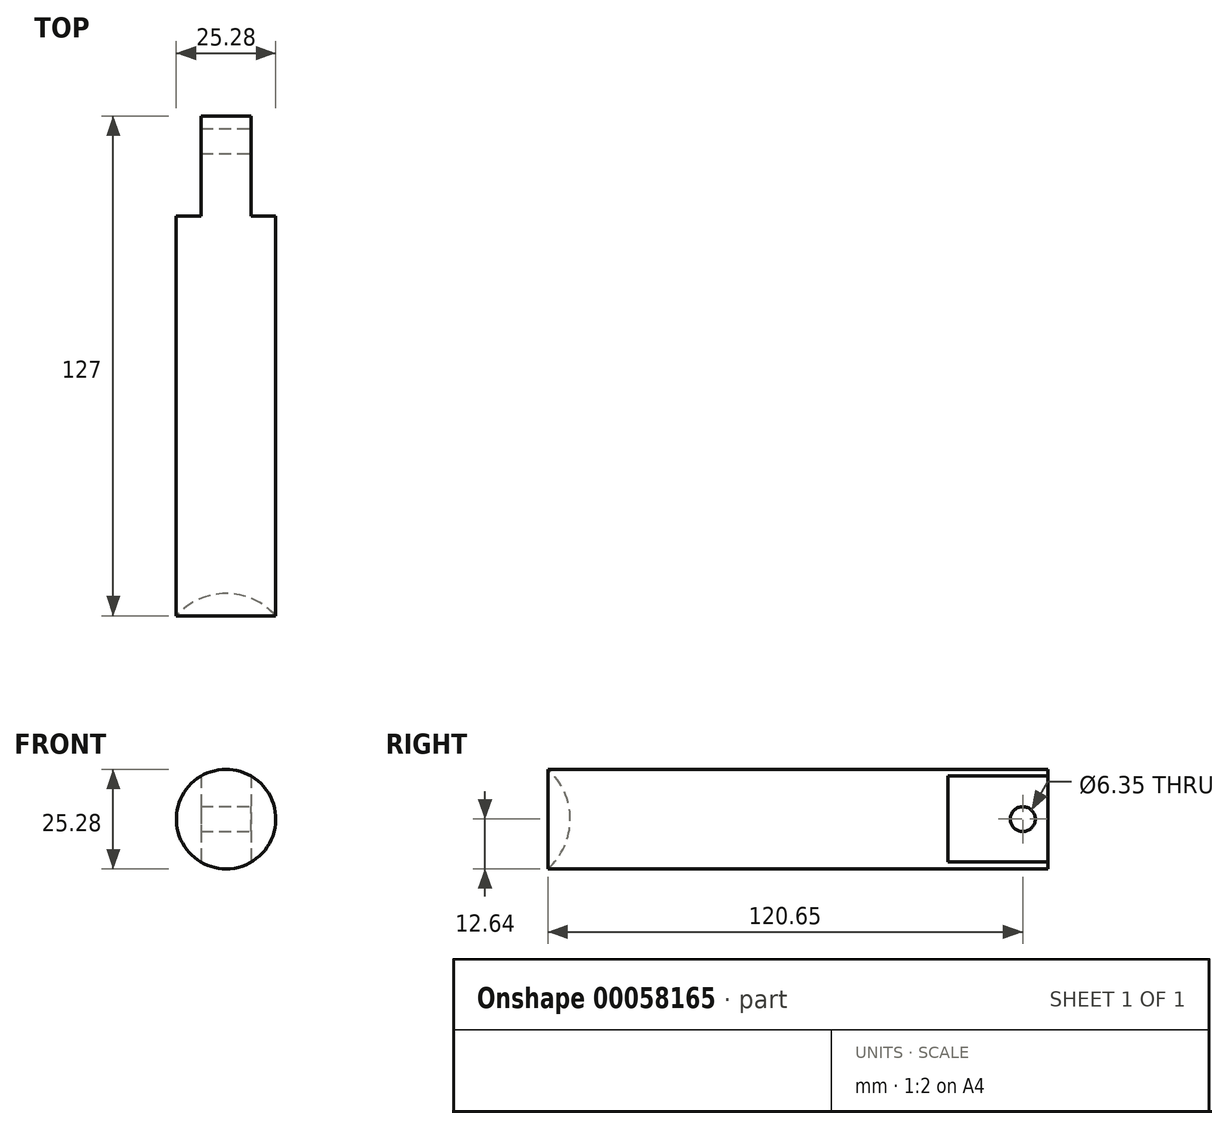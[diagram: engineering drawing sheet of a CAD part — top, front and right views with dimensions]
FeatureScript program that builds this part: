
annotation { "Feature Type Name" : "Feature", "Feature Type Description" : "" }
export const myFeature = defineFeature(function(context is Context, id is Id, definition is map)
    precondition{}
    {
        {
            var Q0;
            Q0=qCreatedBy(makeId("Front.planeOp"),FACE);
            var sketch = newSketch(context, id + "F0", { "sketchPlane" : qUnion([Q0])});
            skCircle(sketch, "E0", {"center": v(0, 0) * mm, "radius": 12.64 * mm});
            skSolve(sketch);
        }
        {
            var Q0;
            Q0=makeQuery(id+"F0.imprint","IMPRINT",FACE,{"disambiguationData":[TD([[makeQuery(id+"F0.imprint","IMPRINT",EDGE,{"derivedFrom":sQuery(id+"F0.wireOp",EDGE,"E0")}),1.0]])]});
            extrude(context, id + "F1", {"entities" : qUnion([Q0]), "depth" : 127 * mm});
        }
        {
            var Q0;
            Q0=qCreatedBy(makeId("Top.planeOp"),FACE);
            var sketch = newSketch(context, id + "F2", { "sketchPlane" : qUnion([Q0])});
            skLineSegment(sketch, "E1", {"start": v(6.35, 10.47) * mm, "end": v(6.35, -25.4) * mm});
            skLineSegment(sketch, "E2", {"start": v(6.35, -25.4) * mm, "end": v(27.52, -25.4) * mm});
            skLineSegment(sketch, "E3", {"start": v(27.52, -25.4) * mm, "end": v(27.52, 10.47) * mm});
            skLineSegment(sketch, "E4", {"start": v(27.52, 10.47) * mm, "end": v(6.35, 10.47) * mm});
            skLineSegment(sketch, "E5", {"start": v(0, 43.64) * mm, "end": v(0, 10.15) * mm, "construction": true});
            skLineSegment(sketch, "E6.MirrorCS", {"start": v(-6.35, -25.4) * mm, "end": v(-27.52, -25.4) * mm});
            skLineSegment(sketch, "E7.MirrorCS", {"start": v(-27.52, -25.4) * mm, "end": v(-27.52, 10.47) * mm});
            skLineSegment(sketch, "E8.MirrorCS", {"start": v(-6.35, 10.47) * mm, "end": v(-6.35, -25.4) * mm});
            skLineSegment(sketch, "E9.MirrorCS", {"start": v(-27.52, 10.47) * mm, "end": v(-6.35, 10.47) * mm});
            skSolve(sketch);
        }
        {
            var Q0;
            Q0=makeQuery(id+"F2.imprint","IMPRINT",FACE,{"disambiguationData":[TD([[makeQuery(id+"F2.imprint","IMPRINT",EDGE,{"derivedFrom":sQuery(id+"F2.wireOp",EDGE,"E1")}),1.0]])]});
            var Q1;
            Q1=makeQuery(id+"F2.imprint","IMPRINT",FACE,{"disambiguationData":[TD([[makeQuery(id+"F2.imprint","IMPRINT",EDGE,{"derivedFrom":sQuery(id+"F2.wireOp",EDGE,"E7.MirrorCS")}),-1.0]])]});
            extrude(context, id + "F3", {"entities" : qUnion([Q0, Q1]), "operationType" : NewBodyOperationType.REMOVE, "endBound" : BoundingType.SYMMETRIC, "oppositeDirection" : true, "depth" : 50.8 * mm});
        }
        {
            var Q0;
            Q0=qCreatedBy(makeId("Top.planeOp"),FACE);
            var sketch = newSketch(context, id + "F4", { "sketchPlane" : qUnion([Q0])});
            skArc(sketch, "E10", {"start": v(16.9, -138.22) * mm, "mid": v(0, -121.32) * mm, "end": v(-16.9, -138.22) * mm});
            skLineSegment(sketch, "E11", {"start": v(-12.64, -127) * mm, "end": v(-12.64, -25.4) * mm});
            skLineSegment(sketch, "E12", {"start": v(12.64, -25.4) * mm, "end": v(12.64, -127) * mm});
            skLineSegment(sketch, "E13", {"start": v(0, -138.22) * mm, "end": v(19.38, -138.22) * mm, "construction": true});
            skLineSegment(sketch, "E14", {"start": v(16.9, -138.22) * mm, "end": v(-16.9, -138.22) * mm});
            skSolve(sketch);
        }
        {
            var Q0;
            {var subQ0=sQuery(id+"F4.wireOp",EDGE,"E14");Q0=makeQuery(id+"F4.imprint","IMPRINT",FACE,{"disambiguationData":[TD([[makeQuery(id+"F4.imprint","IMPRINT",EDGE,{"derivedFrom":subQ0}),-1.0]])]});}
            var Q1;
            Q1=sQuery(id+"F4.wireOp",EDGE,"E13");
            revolve(context, id + "F5", {"operationType" : NewBodyOperationType.REMOVE, "entities" : qUnion([Q0]), "axis" : qUnion([Q1]), "revolveType" : RevolveType.FULL, "oppositeDirection" : true});
        }
        {
            var Q0;
            Q0=makeQuery(id+"F3.boolean.opBoolean","COPY",FACE,{"derivedFrom":makeQuery(id+"F3.opExtrude","SWEPT_FACE",FACE,{"disambiguationData":[OSD([sQuery(id+"F2.wireOp",EDGE,"E1")])]})});
            var sketch = newSketch(context, id + "F6", { "sketchPlane" : qUnion([Q0])});
            skCircle(sketch, "E15", {"center": v(-6.35, 0) * mm, "radius": 3.18 * mm});
            skSolve(sketch);
        }
        {
            var Q0;
            Q0=makeQuery(id+"F6.imprint","IMPRINT",FACE,{"disambiguationData":[TD([[makeQuery(id+"F6.imprint","IMPRINT",EDGE,{"derivedFrom":sQuery(id+"F6.wireOp",EDGE,"E15")}),1.0]])]});
            extrude(context, id + "F7", {"entities" : qUnion([Q0]), "operationType" : NewBodyOperationType.REMOVE, "endBound" : BoundingType.THROUGH_ALL, "oppositeDirection" : true, "depth" : 25.4 * mm});
        }
    });
